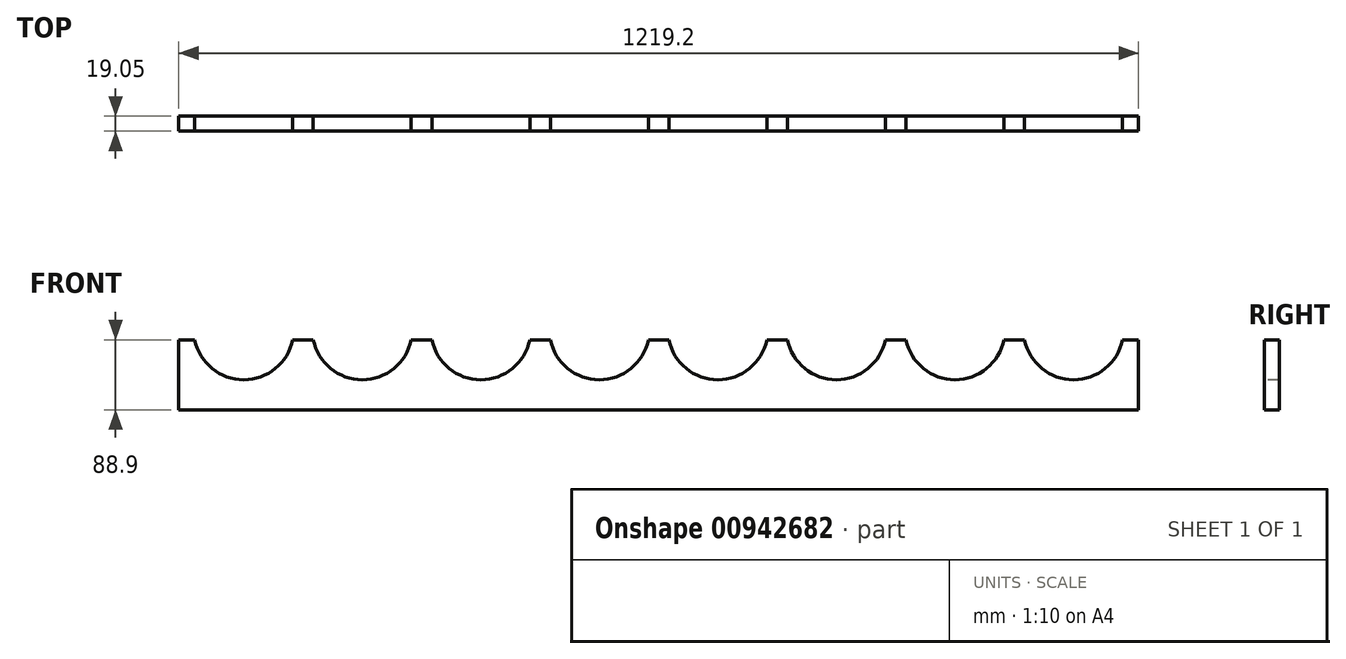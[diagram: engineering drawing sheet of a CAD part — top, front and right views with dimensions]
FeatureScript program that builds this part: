
annotation { "Feature Type Name" : "Feature", "Feature Type Description" : "" }
export const myFeature = defineFeature(function(context is Context, id is Id, definition is map)
    precondition{}
    {
        {
            var Q0;
            Q0=qCreatedBy(makeId("Front.planeOp"),FACE);
            var sketch = newSketch(context, id + "F0", { "sketchPlane" : qUnion([Q0])});
            skLineSegment(sketch, "E0.bottom", {"start": v(609.6, -44.45) * mm, "end": v(-609.6, -44.45) * mm});
            skLineSegment(sketch, "E0.top", {"start": v(609.6, 44.45) * mm, "end": v(589.27, 44.45) * mm});
            skLineSegment(sketch, "E0.left", {"start": v(609.6, -44.45) * mm, "end": v(609.6, 44.45) * mm});
            skLineSegment(sketch, "E0.right", {"start": v(-609.6, -44.45) * mm, "end": v(-609.6, 44.45) * mm});
            skPoint(sketch, "E0.middle", {"position": v(0, 0) * mm});
            skArc(sketch, "E1", {"start": v(-589.27, 44.45) * mm, "mid": v(-520.67, -6.03) * mm, "end": v(-463.55, 57.15) * mm});
            skArc(sketch, "E2.1.0.0", {"start": v(-439.96, 57.15) * mm, "mid": v(-382.85, -6.03) * mm, "end": v(-314.25, 44.45) * mm});
            skArc(sketch, "E2.2.0.0", {"start": v(-288.1, 44.45) * mm, "mid": v(-225.88, -6.35) * mm, "end": v(-163.66, 44.45) * mm});
            skArc(sketch, "E2.3.0.0", {"start": v(-137.5, 44.45) * mm, "mid": v(-75.3, -6.35) * mm, "end": v(-13.08, 44.45) * mm});
            skArc(sketch, "E2.4.0.0", {"start": v(13.08, 44.45) * mm, "mid": v(75.3, -6.35) * mm, "end": v(137.5, 44.45) * mm});
            skArc(sketch, "E2.5.0.0", {"start": v(163.66, 44.45) * mm, "mid": v(225.88, -6.35) * mm, "end": v(288.1, 44.45) * mm});
            skArc(sketch, "E2.6.0.0", {"start": v(314.25, 44.45) * mm, "mid": v(376.46, -6.35) * mm, "end": v(438.68, 44.45) * mm});
            skArc(sketch, "E2.7.0.0", {"start": v(464.83, 44.45) * mm, "mid": v(527.05, -6.35) * mm, "end": v(589.27, 44.45) * mm});
            skLineSegment(sketch, "E2.direction1", {"start": v(-527.05, 57.15) * mm, "end": v(-376.46, 57.15) * mm, "construction": true});
            skLineSegment(sketch, "E3.trimOffspring", {"start": v(464.83, 44.45) * mm, "end": v(438.68, 44.45) * mm});
            skLineSegment(sketch, "E4.trimOffspring", {"start": v(314.25, 44.45) * mm, "end": v(288.1, 44.45) * mm});
            skLineSegment(sketch, "E5.trimOffspring", {"start": v(163.66, 44.45) * mm, "end": v(137.5, 44.45) * mm});
            skLineSegment(sketch, "E6.trimOffspring", {"start": v(13.08, 44.45) * mm, "end": v(-13.08, 44.45) * mm});
            skLineSegment(sketch, "E7.trimOffspring", {"start": v(-137.5, 44.45) * mm, "end": v(-163.66, 44.45) * mm});
            skLineSegment(sketch, "E8.trimOffspring", {"start": v(-288.1, 44.45) * mm, "end": v(-314.25, 44.45) * mm});
            skLineSegment(sketch, "E9.trimOffspring", {"start": v(-438.68, 44.45) * mm, "end": v(-464.83, 44.45) * mm});
            skLineSegment(sketch, "E10.trimOffspring", {"start": v(-589.27, 44.45) * mm, "end": v(-609.6, 44.45) * mm});
            skSolve(sketch);
        }
        {
            var Q0;
            Q0=makeQuery(id+"F0.imprint","IMPRINT",FACE,{"disambiguationData":[TD([[makeQuery(id+"F0.imprint","IMPRINT",EDGE,{"derivedFrom":sQuery(id+"F0.wireOp",EDGE,"E0.bottom")}),-1.0]])]});
            extrude(context, id + "F1", {"entities" : qUnion([Q0]), "oppositeDirection" : true, "depth" : 19.05 * mm, "offsetDistance" : 25.4 * mm});
        }
    });
